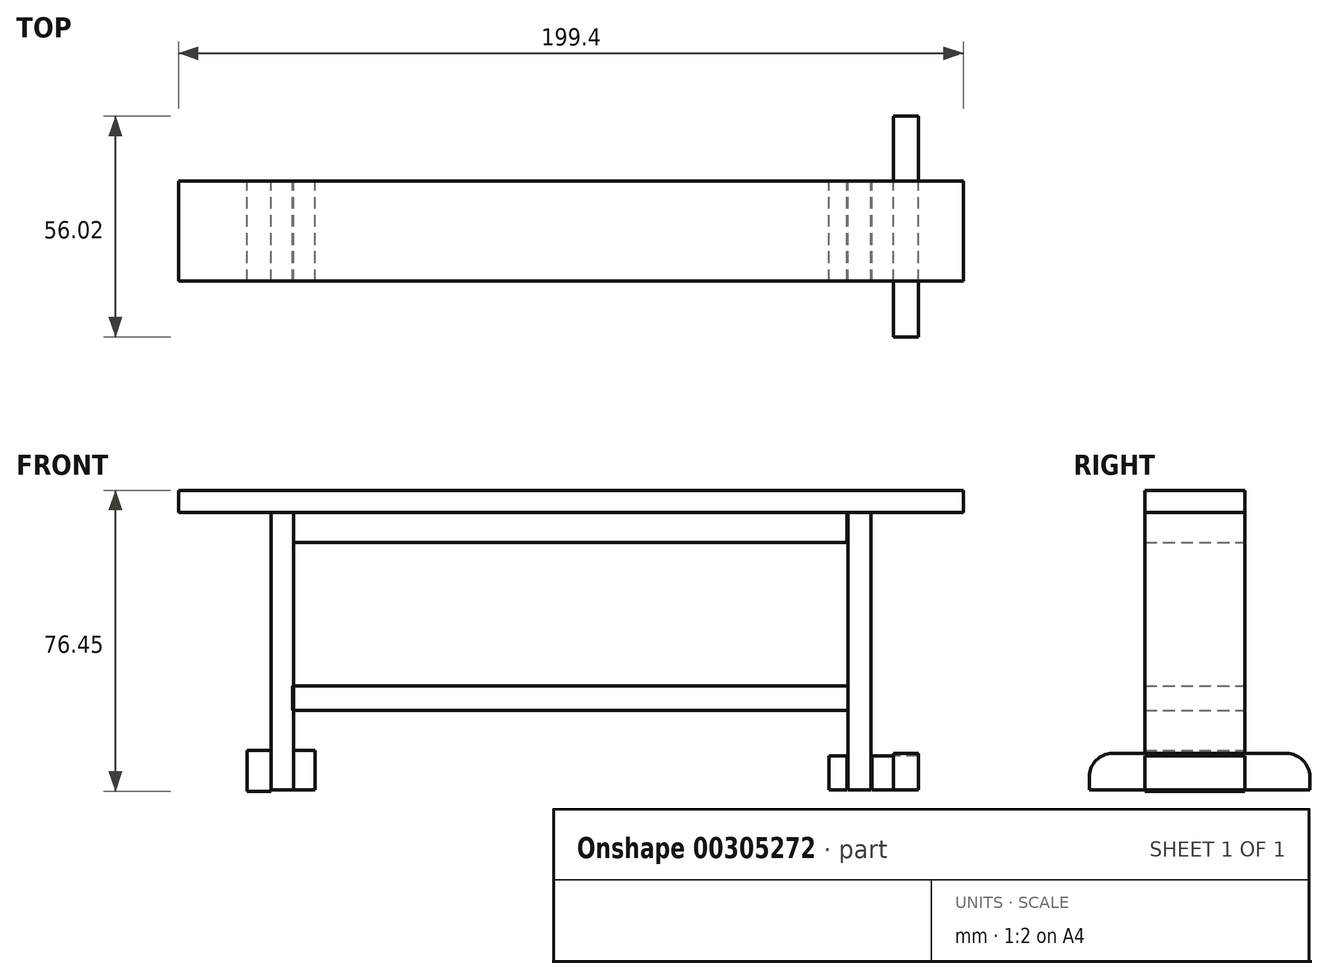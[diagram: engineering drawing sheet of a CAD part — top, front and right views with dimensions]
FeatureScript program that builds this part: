
annotation { "Feature Type Name" : "Feature", "Feature Type Description" : "" }
export const myFeature = defineFeature(function(context is Context, id is Id, definition is map)
    precondition{}
    {
        {
            var Q0;
            Q0=qCreatedBy(makeId("Front.planeOp"),FACE);
            var sketch = newSketch(context, id + "F0", { "sketchPlane" : qUnion([Q0])});
            skLineSegment(sketch, "E0.bottom", {"start": v(-99.7, 0) * mm, "end": v(99.7, 0) * mm});
            skLineSegment(sketch, "E0.top", {"start": v(-99.7, -5.6) * mm, "end": v(99.7, -5.6) * mm});
            skLineSegment(sketch, "E0.left", {"start": v(-99.7, 0) * mm, "end": v(-99.7, -5.6) * mm});
            skLineSegment(sketch, "E0.right", {"start": v(99.7, 0) * mm, "end": v(99.7, -5.6) * mm});
            skSolve(sketch);
        }
        {
            var Q0;
            Q0=qCreatedBy(makeId("Front.planeOp"),FACE);
            var sketch = newSketch(context, id + "F1", { "sketchPlane" : qUnion([Q0])});
            skLineSegment(sketch, "E1.bottom", {"start": v(-76.18, -5.6) * mm, "end": v(-70.44, -5.6) * mm});
            skLineSegment(sketch, "E1.top", {"start": v(-76.18, -76.18) * mm, "end": v(-70.44, -76.18) * mm});
            skLineSegment(sketch, "E1.left", {"start": v(-76.18, -5.6) * mm, "end": v(-76.18, -76.18) * mm});
            skLineSegment(sketch, "E1.right", {"start": v(-70.44, -5.6) * mm, "end": v(-70.44, -76.18) * mm});
            skSolve(sketch);
        }
        {
            var Q0;
            Q0=qCreatedBy(makeId("Front.planeOp"),FACE);
            var sketch = newSketch(context, id + "F2", { "sketchPlane" : qUnion([Q0])});
            skLineSegment(sketch, "E2.bottom", {"start": v(70.44, -5.6) * mm, "end": v(76.18, -5.6) * mm});
            skLineSegment(sketch, "E2.top", {"start": v(70.44, -76.18) * mm, "end": v(76.18, -76.18) * mm});
            skLineSegment(sketch, "E2.left", {"start": v(70.44, -5.6) * mm, "end": v(70.44, -76.18) * mm});
            skLineSegment(sketch, "E2.right", {"start": v(76.18, -5.6) * mm, "end": v(76.18, -76.18) * mm});
            skSolve(sketch);
        }
        {
            var Q0;
            Q0=qCreatedBy(makeId("Front.planeOp"),FACE);
            var sketch = newSketch(context, id + "F3", { "sketchPlane" : qUnion([Q0])});
            skLineSegment(sketch, "E3.bottom", {"start": v(-76.18, -66.06) * mm, "end": v(-82.2, -66.06) * mm});
            skLineSegment(sketch, "E3.top", {"start": v(-76.18, -76.45) * mm, "end": v(-82.2, -76.45) * mm});
            skLineSegment(sketch, "E3.left", {"start": v(-76.18, -66.06) * mm, "end": v(-76.18, -76.45) * mm});
            skLineSegment(sketch, "E3.right", {"start": v(-82.2, -66.06) * mm, "end": v(-82.2, -76.45) * mm});
            skSolve(sketch);
        }
        {
            var Q0;
            Q0=qCreatedBy(makeId("Front.planeOp"),FACE);
            var sketch = newSketch(context, id + "F4", { "sketchPlane" : qUnion([Q0])});
            skLineSegment(sketch, "E4.bottom", {"start": v(-70.44, -66.06) * mm, "end": v(-64.97, -66.06) * mm});
            skLineSegment(sketch, "E4.top", {"start": v(-70.44, -76.18) * mm, "end": v(-64.97, -76.18) * mm});
            skLineSegment(sketch, "E4.left", {"start": v(-70.44, -66.06) * mm, "end": v(-70.44, -76.18) * mm});
            skLineSegment(sketch, "E4.right", {"start": v(-64.97, -66.06) * mm, "end": v(-64.97, -76.18) * mm});
            skSolve(sketch);
        }
        {
            var Q0;
            Q0=qCreatedBy(makeId("Front.planeOp"),FACE);
            var sketch = newSketch(context, id + "F5", { "sketchPlane" : qUnion([Q0])});
            skLineSegment(sketch, "E5.bottom", {"start": v(76.45, -67.43) * mm, "end": v(81.92, -67.43) * mm});
            skLineSegment(sketch, "E5.top", {"start": v(76.45, -76.18) * mm, "end": v(81.92, -76.18) * mm});
            skLineSegment(sketch, "E5.left", {"start": v(76.45, -67.43) * mm, "end": v(76.45, -76.18) * mm});
            skLineSegment(sketch, "E5.right", {"start": v(81.92, -67.43) * mm, "end": v(81.92, -76.18) * mm});
            skSolve(sketch);
        }
        {
            var Q0;
            Q0=qCreatedBy(makeId("Front.planeOp"),FACE);
            var sketch = newSketch(context, id + "F6", { "sketchPlane" : qUnion([Q0])});
            skLineSegment(sketch, "E6.bottom", {"start": v(70.16, -67.43) * mm, "end": v(65.51, -67.43) * mm});
            skLineSegment(sketch, "E6.top", {"start": v(70.16, -76.18) * mm, "end": v(65.51, -76.18) * mm});
            skLineSegment(sketch, "E6.left", {"start": v(70.16, -67.43) * mm, "end": v(70.16, -76.18) * mm});
            skLineSegment(sketch, "E6.right", {"start": v(65.51, -67.43) * mm, "end": v(65.51, -76.18) * mm});
            skSolve(sketch);
        }
        {
            var Q0;
            Q0=qCreatedBy(makeId("Front.planeOp"),FACE);
            var sketch = newSketch(context, id + "F7", { "sketchPlane" : qUnion([Q0])});
            skLineSegment(sketch, "E7.bottom", {"start": v(-70.7, -49.65) * mm, "end": v(70.44, -49.65) * mm});
            skLineSegment(sketch, "E7.top", {"start": v(-70.7, -55.94) * mm, "end": v(70.44, -55.94) * mm});
            skLineSegment(sketch, "E7.left", {"start": v(-70.7, -49.65) * mm, "end": v(-70.7, -55.94) * mm});
            skLineSegment(sketch, "E7.right", {"start": v(70.44, -49.65) * mm, "end": v(70.44, -55.94) * mm});
            skSolve(sketch);
        }
        {
            var Q0;
            Q0=qCreatedBy(makeId("Front.planeOp"),FACE);
            var sketch = newSketch(context, id + "F8", { "sketchPlane" : qUnion([Q0])});
            skLineSegment(sketch, "E8.bottom", {"start": v(-70.44, -5.6) * mm, "end": v(70.16, -5.6) * mm});
            skLineSegment(sketch, "E8.top", {"start": v(-70.44, -13.27) * mm, "end": v(70.16, -13.27) * mm});
            skLineSegment(sketch, "E8.left", {"start": v(-70.44, -5.6) * mm, "end": v(-70.44, -13.27) * mm});
            skLineSegment(sketch, "E8.right", {"start": v(70.16, -5.6) * mm, "end": v(70.16, -13.27) * mm});
            skSolve(sketch);
        }
        {
            var Q0;
            Q0 = qSketchRegion(id + "F0", true);
            var Q1;
            Q1 = qSketchRegion(id + "F1", true);
            var Q2;
            Q2 = qSketchRegion(id + "F2", true);
            var Q3;
            Q3 = qSketchRegion(id + "F3", true);
            var Q4;
            Q4 = qSketchRegion(id + "F4", true);
            var Q5;
            Q5 = qSketchRegion(id + "F5", true);
            var Q6;
            Q6 = qSketchRegion(id + "F6", true);
            var Q7;
            Q7 = qSketchRegion(id + "F7", true);
            var Q8;
            Q8 = qSketchRegion(id + "F8", true);
            extrude(context, id + "F9", {"entities" : qUnion([Q0, Q1, Q2, Q3, Q4, Q5, Q6, Q7, Q8]), "depth" : 25.4 * mm});
        }
        {
            var Q0;
            Q0=makeQuery(id+"F9.opExtrude","SWEPT_FACE",FACE,{"disambiguationData":[OSD([sQuery(id+"F5.wireOp",EDGE,"E5.right")])]});
            var sketch = newSketch(context, id + "F10", { "sketchPlane" : qUnion([Q0])});
            skLineSegment(sketch, "E9.bottom", {"start": v(-33.64, -66.87) * mm, "end": v(10.56, -66.87) * mm});
            skLineSegment(sketch, "E9.top", {"start": v(-39.55, -76.18) * mm, "end": v(16.47, -76.18) * mm});
            skLineSegment(sketch, "E9.left", {"start": v(-39.55, -72.78) * mm, "end": v(-39.55, -76.18) * mm});
            skLineSegment(sketch, "E9.right", {"start": v(16.47, -72.78) * mm, "end": v(16.47, -76.18) * mm});
            skPoint(sketch, "E10.visualSharp", {"position": v(-39.55, -66.87) * mm});
            skArc(sketch, "E10.filletArc", {"start": v(-33.64, -66.87) * mm, "mid": v(-37.82, -68.6) * mm, "end": v(-39.55, -72.78) * mm});
            skPoint(sketch, "E11.visualSharp", {"position": v(16.47, -66.87) * mm});
            skArc(sketch, "E11.filletArc", {"start": v(16.47, -72.78) * mm, "mid": v(14.74, -68.6) * mm, "end": v(10.56, -66.87) * mm});
            skSolve(sketch);
        }
        {
            var Q0;
            Q0=makeQuery(id+"F10.imprint","IMPRINT",FACE,{"disambiguationData":[TD([[makeQuery(id+"F10.imprint","IMPRINT",EDGE,{"derivedFrom":sQuery(id+"F10.wireOp",EDGE,"E9.bottom")}),-1.0]])]});
            extrude(context, id + "F11", {"entities" : qUnion([Q0]), "depth" : 6.35 * mm});
        }
        {
            var Q0;
            Q0=makeQuery(id+"F11.opExtrude","SWEPT_BODY",BODY,{"disambiguationData":[OSD([sQuery(id+"F5.wireOp",EDGE,"E5.bottom"),sQuery(id+"F5.wireOp",EDGE,"E5.right"),sQuery(id+"F10.wireOp",EDGE,"E9.bottom"),sQuery(id+"F10.wireOp",EDGE,"E9.top"),sQuery(id+"F10.wireOp",EDGE,"E9.left"),sQuery(id+"F10.wireOp",EDGE,"E9.right"),sQuery(id+"F10.wireOp",EDGE,"E10.filletArc"),sQuery(id+"F10.wireOp",EDGE,"E11.filletArc")])]});
            transform(context, id + "F12", {"entities" : qUnion([Q0]), "transformType" : TransformType.TRANSLATION_3D, "dx" : 0 * mm, "dy" : 0 * mm, "dz" : 0 * mm, "makeCopy" : true});
        }
    });
